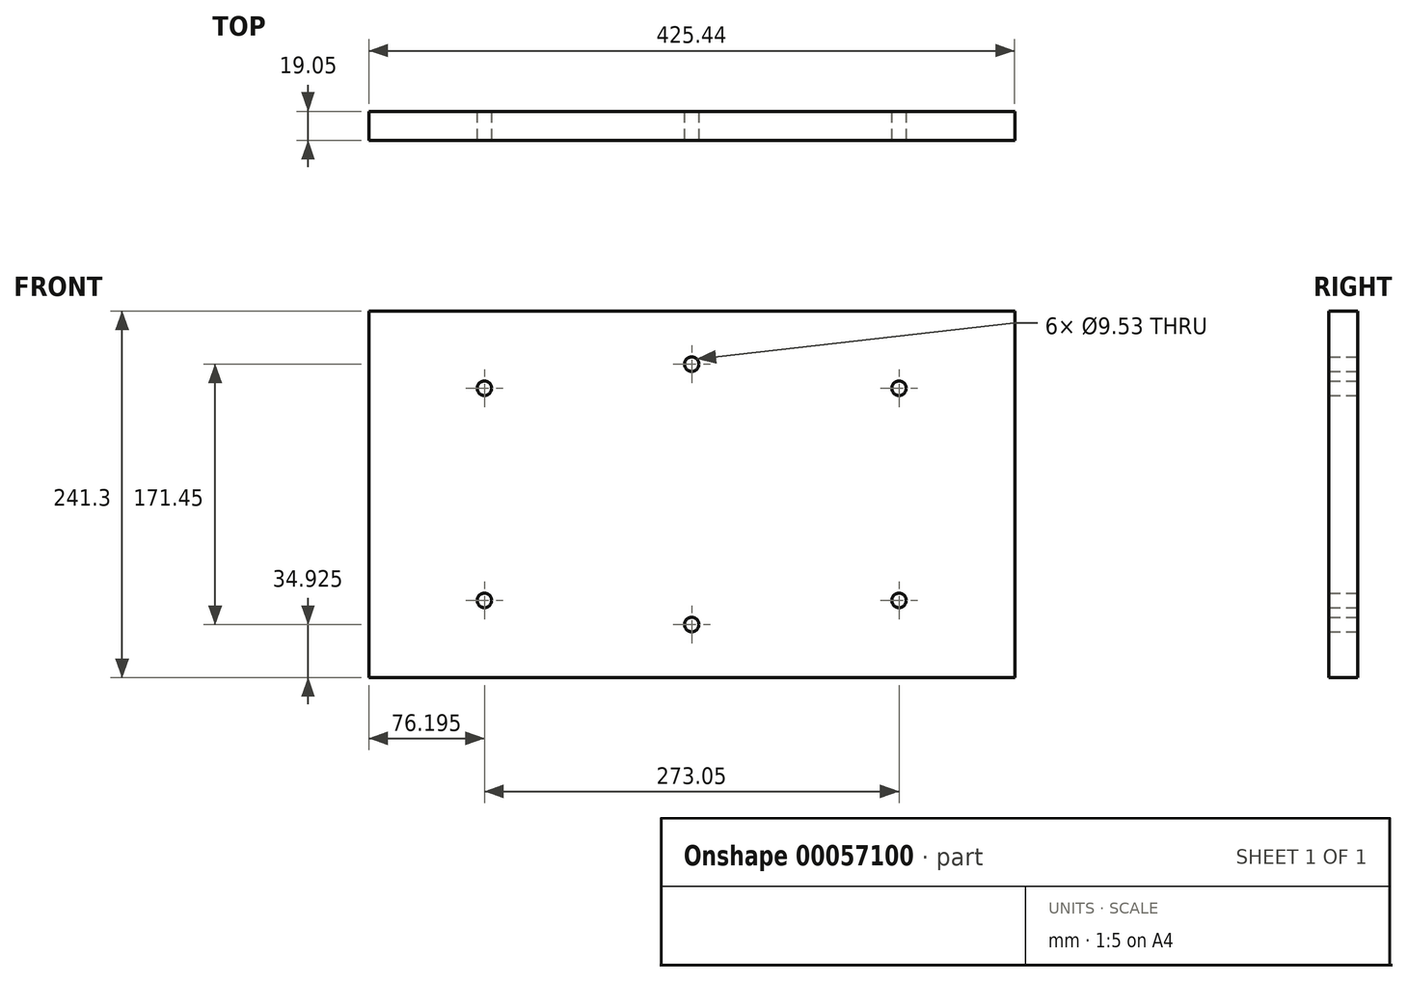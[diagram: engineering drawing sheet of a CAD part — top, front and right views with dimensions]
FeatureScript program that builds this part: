
annotation { "Feature Type Name" : "Feature", "Feature Type Description" : "" }
export const myFeature = defineFeature(function(context is Context, id is Id, definition is map)
    precondition{}
    {
        {
            var Q0;
            Q0=qCreatedBy(makeId("Front.planeOp"),FACE);
            var sketch = newSketch(context, id + "F0", { "sketchPlane" : qUnion([Q0])});
            skLineSegment(sketch, "E0.rect.bottom", {"start": v(-212.72, 120.65) * mm, "end": v(212.73, 120.65) * mm});
            skLineSegment(sketch, "E0.rect.top", {"start": v(-212.73, -120.65) * mm, "end": v(212.72, -120.65) * mm});
            skLineSegment(sketch, "E0.rect.left", {"start": v(-212.72, 120.65) * mm, "end": v(-212.73, -120.65) * mm});
            skLineSegment(sketch, "E0.rect.right", {"start": v(212.73, 120.65) * mm, "end": v(212.72, -120.65) * mm});
            skPoint(sketch, "E0.rect.middle", {"position": v(0, 0) * mm});
            skLineSegment(sketch, "E1.rect.bottom", {"start": v(-136.53, 69.85) * mm, "end": v(136.53, 69.85) * mm, "construction": true});
            skLineSegment(sketch, "E1.rect.top", {"start": v(-136.53, -69.85) * mm, "end": v(136.53, -69.85) * mm, "construction": true});
            skLineSegment(sketch, "E1.rect.left", {"start": v(-136.53, 69.85) * mm, "end": v(-136.53, -69.85) * mm, "construction": true});
            skLineSegment(sketch, "E1.rect.right", {"start": v(136.53, 69.85) * mm, "end": v(136.53, -69.85) * mm, "construction": true});
            skLineSegment(sketch, "E2", {"start": v(0, -85.73) * mm, "end": v(0, 85.73) * mm, "construction": true});
            skSolve(sketch);
        }
        {
            var Q0;
            Q0 = qSketchRegion(id + "F0", true);
            extrude(context, id + "F1", {"entities" : qUnion([Q0]), "depth" : 19.05 * mm});
        }
        {
            var Q0;
            Q0=sQuery(id+"F0.wireOp",VERTEX,"E1.rect.right.start");
            var Q1;
            Q1=makeQuery(id+"F1.opExtrude","SWEPT_BODY",BODY,{"disambiguationData":[OSD([sQuery(id+"F0.wireOp",EDGE,"E0.rect.bottom"),sQuery(id+"F0.wireOp",EDGE,"E0.rect.top"),sQuery(id+"F0.wireOp",EDGE,"E0.rect.left"),sQuery(id+"F0.wireOp",EDGE,"E0.rect.right")])]});
            hole(context, id + "F2", {"style" : HoleStyle.SIMPLE, "holeDiameter" : 9.52 * mm, "endStyle" : HoleEndStyle.THROUGH, "oppositeDirection" : true, "locations" : qUnion([Q0]), "scope" : qUnion([Q1])});
        }
        {
            var Q0;
            Q0=sQuery(id+"F0.wireOp",VERTEX,"E1.rect.right.end");
            var Q1;
            Q1=makeQuery(id+"F1.opExtrude","SWEPT_BODY",BODY,{"disambiguationData":[OSD([sQuery(id+"F0.wireOp",EDGE,"E0.rect.bottom"),sQuery(id+"F0.wireOp",EDGE,"E0.rect.top"),sQuery(id+"F0.wireOp",EDGE,"E0.rect.left"),sQuery(id+"F0.wireOp",EDGE,"E0.rect.right")])]});
            hole(context, id + "F3", {"style" : HoleStyle.SIMPLE, "holeDiameter" : 9.52 * mm, "endStyle" : HoleEndStyle.THROUGH, "oppositeDirection" : true, "locations" : qUnion([Q0]), "scope" : qUnion([Q1])});
        }
        {
            var Q0;
            Q0=sQuery(id+"F0.wireOp",VERTEX,"E1.rect.left.start");
            var Q1;
            Q1=makeQuery(id+"F1.opExtrude","SWEPT_BODY",BODY,{"disambiguationData":[OSD([sQuery(id+"F0.wireOp",EDGE,"E0.rect.bottom"),sQuery(id+"F0.wireOp",EDGE,"E0.rect.top"),sQuery(id+"F0.wireOp",EDGE,"E0.rect.left"),sQuery(id+"F0.wireOp",EDGE,"E0.rect.right")])]});
            hole(context, id + "F4", {"style" : HoleStyle.SIMPLE, "holeDiameter" : 9.52 * mm, "endStyle" : HoleEndStyle.THROUGH, "oppositeDirection" : true, "locations" : qUnion([Q0]), "scope" : qUnion([Q1])});
        }
        {
            var Q0;
            Q0=sQuery(id+"F0.wireOp",VERTEX,"E1.rect.left.end");
            var Q1;
            Q1=makeQuery(id+"F1.opExtrude","SWEPT_BODY",BODY,{"disambiguationData":[OSD([sQuery(id+"F0.wireOp",EDGE,"E0.rect.bottom"),sQuery(id+"F0.wireOp",EDGE,"E0.rect.top"),sQuery(id+"F0.wireOp",EDGE,"E0.rect.left"),sQuery(id+"F0.wireOp",EDGE,"E0.rect.right")])]});
            hole(context, id + "F5", {"style" : HoleStyle.SIMPLE, "holeDiameter" : 9.52 * mm, "endStyle" : HoleEndStyle.THROUGH, "oppositeDirection" : true, "locations" : qUnion([Q0]), "scope" : qUnion([Q1])});
        }
        {
            var Q0;
            Q0=sQuery(id+"F0.wireOp",VERTEX,"E2.end");
            var Q1;
            Q1=makeQuery(id+"F1.opExtrude","SWEPT_BODY",BODY,{"disambiguationData":[OSD([sQuery(id+"F0.wireOp",EDGE,"E0.rect.bottom"),sQuery(id+"F0.wireOp",EDGE,"E0.rect.top"),sQuery(id+"F0.wireOp",EDGE,"E0.rect.left"),sQuery(id+"F0.wireOp",EDGE,"E0.rect.right")])]});
            hole(context, id + "F6", {"style" : HoleStyle.SIMPLE, "holeDiameter" : 9.52 * mm, "endStyle" : HoleEndStyle.THROUGH, "oppositeDirection" : true, "locations" : qUnion([Q0]), "scope" : qUnion([Q1])});
        }
        {
            var Q0;
            Q0=sQuery(id+"F0.wireOp",VERTEX,"E2.start");
            var Q1;
            Q1=makeQuery(id+"F1.opExtrude","SWEPT_BODY",BODY,{"disambiguationData":[OSD([sQuery(id+"F0.wireOp",EDGE,"E0.rect.bottom"),sQuery(id+"F0.wireOp",EDGE,"E0.rect.top"),sQuery(id+"F0.wireOp",EDGE,"E0.rect.left"),sQuery(id+"F0.wireOp",EDGE,"E0.rect.right")])]});
            hole(context, id + "F7", {"style" : HoleStyle.SIMPLE, "holeDiameter" : 9.52 * mm, "endStyle" : HoleEndStyle.THROUGH, "oppositeDirection" : true, "locations" : qUnion([Q0]), "scope" : qUnion([Q1])});
        }
    });
